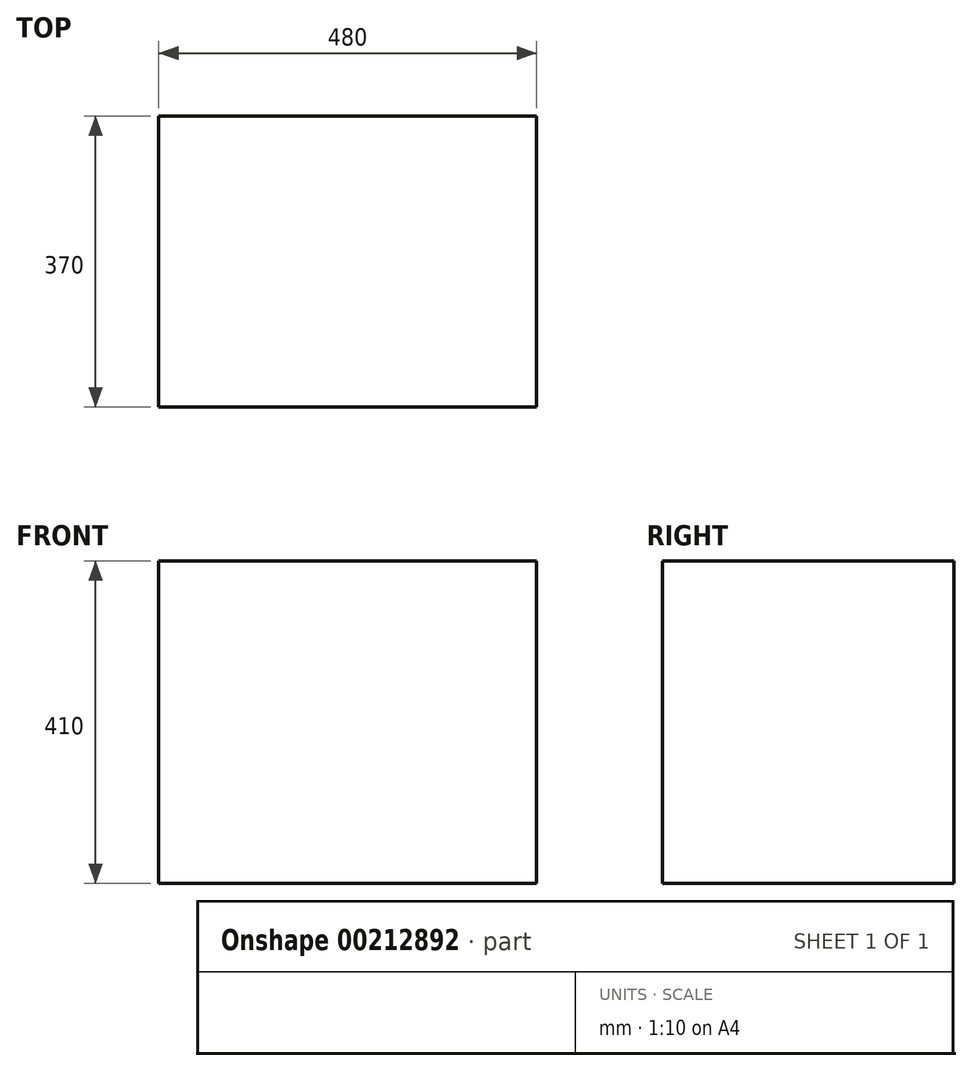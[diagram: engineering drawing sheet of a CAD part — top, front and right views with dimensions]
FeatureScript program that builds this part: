
annotation { "Feature Type Name" : "Feature", "Feature Type Description" : "" }
export const myFeature = defineFeature(function(context is Context, id is Id, definition is map)
    precondition{}
    {
        {
            var Q0;
            Q0=qCreatedBy(makeId("Top.planeOp"),FACE);
            var sketch = newSketch(context, id + "F0", { "sketchPlane" : qUnion([Q0])});
            skLineSegment(sketch, "E0.bottom", {"start": v(0, 0) * mm, "end": v(480, 0) * mm});
            skLineSegment(sketch, "E0.top", {"start": v(0, 370) * mm, "end": v(480, 370) * mm});
            skLineSegment(sketch, "E0.left", {"start": v(0, 0) * mm, "end": v(0, 370) * mm});
            skLineSegment(sketch, "E0.right", {"start": v(480, 0) * mm, "end": v(480, 370) * mm});
            skSolve(sketch);
        }
        {
            var Q0;
            Q0 = qSketchRegion(id + "F0", true);
            extrude(context, id + "F1", {"entities" : qUnion([Q0]), "depth" : 410 * mm});
        }
    });
